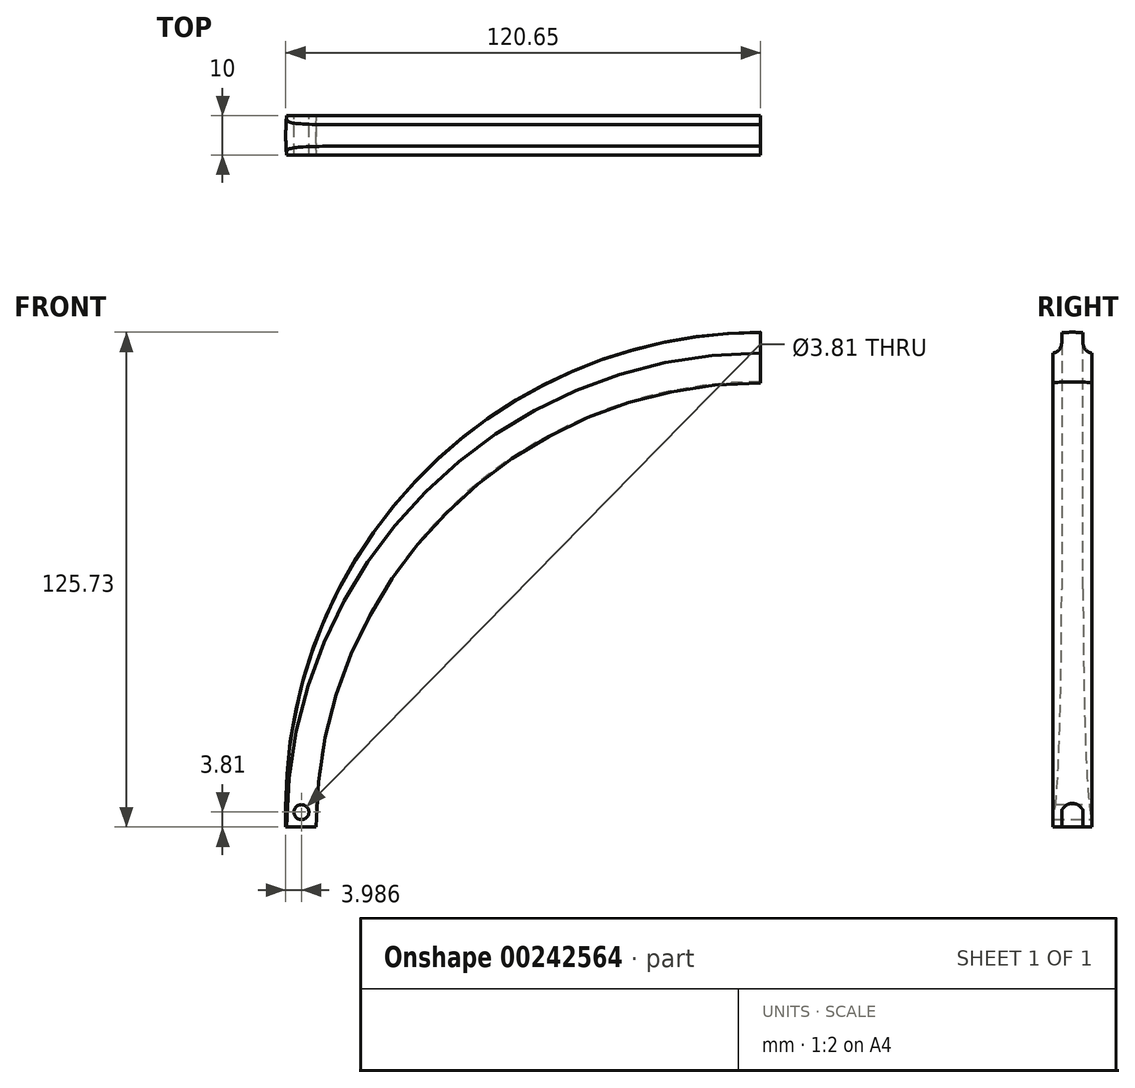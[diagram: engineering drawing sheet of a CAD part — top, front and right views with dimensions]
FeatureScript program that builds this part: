
annotation { "Feature Type Name" : "Feature", "Feature Type Description" : "" }
export const myFeature = defineFeature(function(context is Context, id is Id, definition is map)
    precondition{}
    {
        {
            var Q0;
            Q0=qCreatedBy(makeId("Top.planeOp"),FACE);
            var sketch = newSketch(context, id + "F0", { "sketchPlane" : qUnion([Q0])});
            skLineSegment(sketch, "E0.bottom", {"start": v(0, 5) * mm, "end": v(-31.75, 5) * mm});
            skLineSegment(sketch, "E0.top", {"start": v(0, -5) * mm, "end": v(-31.75, -5) * mm});
            skLineSegment(sketch, "E0.left", {"start": v(0, 5) * mm, "end": v(0, -5) * mm});
            skLineSegment(sketch, "E0.right", {"start": v(-31.75, 5) * mm, "end": v(-31.75, -5) * mm});
            skCircle(sketch, "E1", {"center": v(-63.5, 0) * mm, "radius": 57.15 * mm});
            skLineSegment(sketch, "E2", {"start": v(-63.5, 0) * mm, "end": v(-39.35, 51.8) * mm});
            skLineSegment(sketch, "E3", {"start": v(-63.5, 0) * mm, "end": v(-39.35, -51.8) * mm});
            skCircle(sketch, "E4", {"center": v(-63.5, 0) * mm, "radius": 49.65 * mm});
            skLineSegment(sketch, "E5.bottom", {"start": v(-120.43, -5) * mm, "end": v(-94.98, -5) * mm});
            skLineSegment(sketch, "E5.top", {"start": v(-120.43, 5) * mm, "end": v(-94.98, 5) * mm});
            skLineSegment(sketch, "E5.left", {"start": v(-120.43, -5) * mm, "end": v(-120.43, 5) * mm});
            skLineSegment(sketch, "E5.right", {"start": v(-94.98, -5) * mm, "end": v(-94.98, 5) * mm});
            skPoint(sketch, "E5.middle", {"position": v(-107.7, 0) * mm});
            skLineSegment(sketch, "E6.bottom", {"start": v(-112.9, -5) * mm, "end": v(-115.44, -5) * mm});
            skLineSegment(sketch, "E6.top", {"start": v(-112.9, 5) * mm, "end": v(-115.44, 5) * mm});
            skLineSegment(sketch, "E6.left", {"start": v(-112.9, -5) * mm, "end": v(-112.9, 5) * mm});
            skLineSegment(sketch, "E7", {"start": v(-115.44, -5) * mm, "end": v(-109.06, -19.72) * mm});
            skLineSegment(sketch, "E8", {"start": v(-115.44, 5) * mm, "end": v(-109.06, 19.72) * mm});
            skSolve(sketch);
        }
        {
            var Q0;
            {var subQ5=sQuery(id+"F0.wireOp",EDGE,"E5.left");Q0=makeQuery(id+"F0.imprint","IMPRINT",FACE,{"disambiguationData":[TD([[makeQuery(id+"F0.imprint","IMPRINT",EDGE,{"derivedFrom":subQ5}),-1.0]])]});}
            var Q1;
            {var subQ0=sQuery(id+"F0.wireOp",EDGE,"E5.left");Q1=makeQuery(id+"F0.imprint","IMPRINT",FACE,{"disambiguationData":[TD([[makeQuery(id+"F0.imprint","IMPRINT",EDGE,{"derivedFrom":subQ0}),1.0]])]});}
            var Q2;
            Q2=sQuery(id+"F0.wireOp",EDGE,"E0.left");
            revolve(context, id + "F1", {"entities" : qUnion([Q0, Q1]), "axis" : qUnion([Q2]), "revolveType" : RevolveType.ONE_DIRECTION, "oppositeDirection" : true, "angle" : 90 * degree});
        }
        {
            var Q0;
            Q0=qCreatedBy(makeId("Top.planeOp"),FACE);
            var sketch = newSketch(context, id + "F2", { "sketchPlane" : qUnion([Q0])});
            skLineSegment(sketch, "E9.bottom", {"start": v(-120.59, -2.72) * mm, "end": v(-113, -2.72) * mm});
            skLineSegment(sketch, "E9.top", {"start": v(-120.59, 2.72) * mm, "end": v(-113, 2.72) * mm});
            skLineSegment(sketch, "E9.left", {"start": v(-120.59, -2.72) * mm, "end": v(-120.59, 2.72) * mm});
            skLineSegment(sketch, "E9.right", {"start": v(-113, -2.72) * mm, "end": v(-113, 2.72) * mm});
            skPoint(sketch, "E9.middle", {"position": v(-116.79, 0) * mm});
            skCircle(sketch, "E10.0", {"center": v(-63.5, 0) * mm, "radius": 57.15 * mm});
            skCircle(sketch, "E11.0", {"center": v(-63.5, 0) * mm, "radius": 49.65 * mm});
            skLineSegment(sketch, "E12.0", {"start": v(-113, -5) * mm, "end": v(-113, 5) * mm});
            skSolve(sketch);
        }
        {
            var Q0;
            {var subQ0=sQuery(id+"F2.wireOp",EDGE,"E9.bottom");Q0=makeQuery(id+"F2.imprint","IMPRINT",FACE,{"disambiguationData":[TD([[makeQuery(id+"F2.imprint","IMPRINT",EDGE,{"derivedFrom":subQ0}),1.0]])]});}
            var Q1;
            {var subQ0=sQuery(id+"F2.wireOp",EDGE,"E9.left");Q1=makeQuery(id+"F2.imprint","IMPRINT",FACE,{"disambiguationData":[TD([[makeQuery(id+"F2.imprint","IMPRINT",EDGE,{"derivedFrom":subQ0}),1.0]])]});}
            var Q2;
            Q2=sQuery(id+"F0.wireOp",EDGE,"E0.left");
            revolve(context, id + "F3", {"entities" : qUnion([Q0, Q1]), "axis" : qUnion([Q2]), "revolveType" : RevolveType.ONE_DIRECTION, "oppositeDirection" : true, "angle" : 90 * degree});
        }
        {
            var Q0;
            Q0=makeQuery(id+"F3.opRevolve","SWEPT_BODY",BODY,{"disambiguationData":[OSD([sQuery(id+"F2.wireOp",EDGE,"E9.bottom"),sQuery(id+"F2.wireOp",EDGE,"E9.top"),sQuery(id+"F2.wireOp",EDGE,"E10.0"),sQuery(id+"F2.wireOp",EDGE,"E12.0")])]});
            var Q1;
            {var subQ0=sQuery(id+"FOKxyC75vGGqkeP_1.wireOp",EDGE,"dhaBzZlc-24M0-MS8g-sZFZ-AcKM54QzFo5x");var subQ1=sQuery(id+"FOKxyC75vGGqkeP_1.wireOp",EDGE,"61daa003-04e8-4fe0-b4fb-04c8cb687493.0");Q1=makeQuery(id+"FnwXHbgKbiJatCa_2.boolean.opBoolean","MERGE",EDGE,{"derivedFrom":[makeQuery(id+"FgVdwPRYvFfm8fz_1.opExtrude","SWEPT_EDGE",EDGE,{"disambiguationData":[OSD([subQ1,subQ0])]}),makeQuery(id+"FnwXHbgKbiJatCa_2.opExtrude","SWEPT_EDGE",EDGE,{"disambiguationData":[OSD([subQ1,subQ0])]})]});}
            transform(context, id + "F4", {"entities" : qUnion([Q0]), "transformType" : TransformType.TRANSLATION_3D, "dx" : 0 * mm, "dy" : 0 * mm, "dz" : 5.08 * mm, "makeCopy" : false});
        }
        {
            var Q0;
            Q0=makeQuery(id+"F3.opRevolve","CAP_FACE",FACE,{"disambiguationData":[OSD([sQuery(id+"F2.wireOp",EDGE,"E9.bottom"),sQuery(id+"F2.wireOp",EDGE,"E9.top"),sQuery(id+"F2.wireOp",EDGE,"E10.0"),sQuery(id+"F2.wireOp",EDGE,"E12.0")])],"isStart":true});
            var Q1;
            Q1=makeQuery(id+"F1.opRevolve","CAP_FACE",FACE,{"disambiguationData":[OSD([sQuery(id+"F0.wireOp",EDGE,"E1"),sQuery(id+"F0.wireOp",EDGE,"E5.bottom"),sQuery(id+"F0.wireOp",EDGE,"E5.top"),sQuery(id+"F0.wireOp",EDGE,"E6.right")])],"isStart":true});
            extrude(context, id + "F5", {"entities" : qUnion([Q0]), "operationType" : NewBodyOperationType.ADD, "endBound" : BoundingType.UP_TO_SURFACE, "endBoundEntityFace" : qUnion([Q1]), "depth" : 3.8 * mm});
        }
        {
            var Q0;
            Q0=makeQuery(id+"F5.boolean.opBoolean","INTERSECT",EDGE,{"derivedFrom":[makeQuery(id+"F1.opRevolve","SWEPT_FACE",FACE,{"disambiguationData":[OSD([sQuery(id+"F0.wireOp",EDGE,"E1")])]}),makeQuery(id+"F5.opExtrude","SWEPT_FACE",FACE,{"disambiguationData":[OSD([sQuery(id+"F2.wireOp",EDGE,"E9.bottom")])]})]});
            var Q1;
            Q1=makeQuery(id+"F5.boolean.opBoolean","INTERSECT",EDGE,{"derivedFrom":[makeQuery(id+"F1.opRevolve","SWEPT_FACE",FACE,{"disambiguationData":[OSD([sQuery(id+"F0.wireOp",EDGE,"E1")])]}),makeQuery(id+"F5.opExtrude","SWEPT_FACE",FACE,{"disambiguationData":[OSD([sQuery(id+"F2.wireOp",EDGE,"E9.top")])]})]});
            fillet(context, id + "F6", {"entities" : qUnion([Q0, Q1]), "radius" : 2.6 * mm, "tangentPropagation" : true, "allowEdgeOverflow" : false});
        }
        {
            var Q0;
            Q0=qCreatedBy(makeId("Front.planeOp"),FACE);
            var sketch = newSketch(context, id + "F7", { "sketchPlane" : qUnion([Q0])});
            skCircle(sketch, "E13", {"center": v(-116.66, 3.81) * mm, "radius": 1.9 * mm});
            skSolve(sketch);
        }
        {
            var Q0;
            Q0 = qSketchRegion(id + "F7", true);
            var Q1;
            Q1=makeQuery(id+"F1.opRevolve","SWEPT_FACE",FACE,{"disambiguationData":[OSD([sQuery(id+"F0.wireOp",EDGE,"E5.bottom"),sQuery(id+"F0.wireOp",EDGE,"E6.bottom")])]});
            extrude(context, id + "F8", {"entities" : qUnion([Q0]), "operationType" : NewBodyOperationType.REMOVE, "endBound" : BoundingType.SYMMETRIC, "endBoundEntityFace" : qUnion([Q1]), "depth" : 25.4 * mm});
        }
    });
